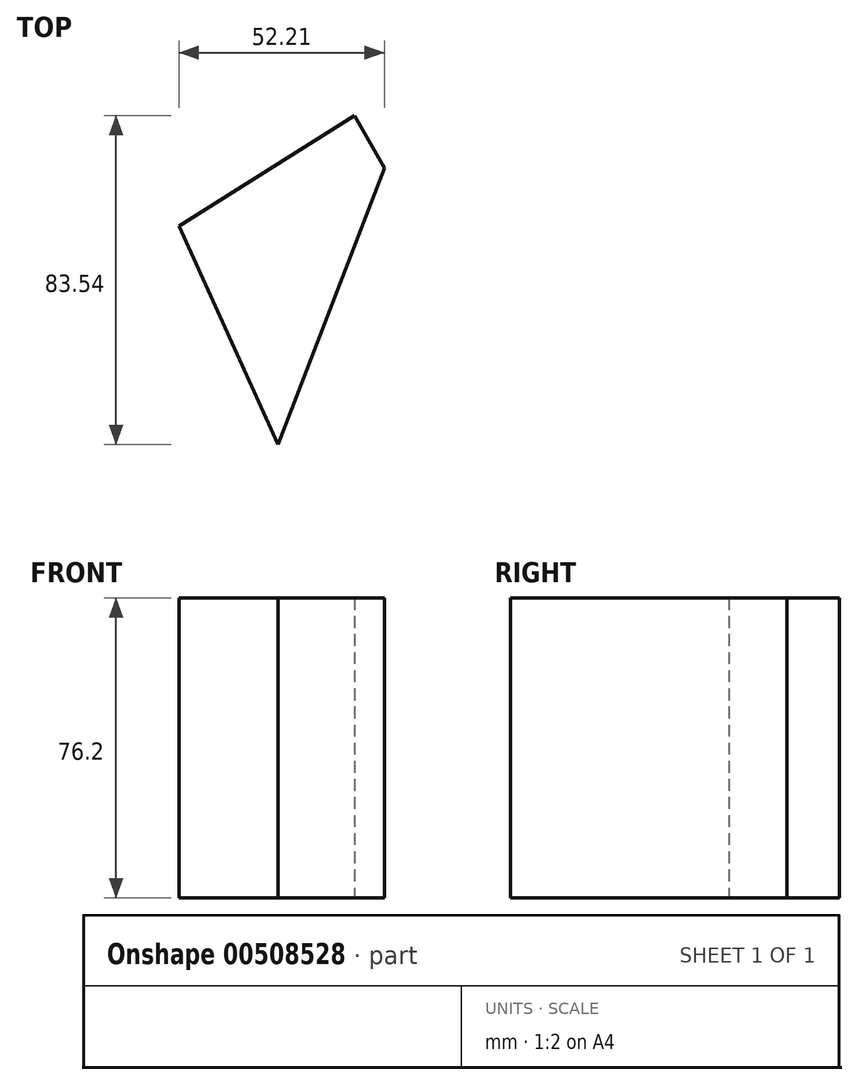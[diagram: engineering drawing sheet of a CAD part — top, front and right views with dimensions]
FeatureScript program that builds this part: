
annotation { "Feature Type Name" : "Feature", "Feature Type Description" : "" }
export const myFeature = defineFeature(function(context is Context, id is Id, definition is map)
    precondition{}
    {
        {
            var Q0;
            Q0=qCreatedBy(makeId("Top.planeOp"),FACE);
            var sketch = newSketch(context, id + "F0", { "sketchPlane" : qUnion([Q0])});
            skLineSegment(sketch, "E0", {"start": v(-44.6, 0) * mm, "end": v(0, 28.08) * mm});
            skLineSegment(sketch, "E1", {"start": v(-19.47, -55.46) * mm, "end": v(7.62, 14.82) * mm});
            skLineSegment(sketch, "E2", {"start": v(7.62, 14.82) * mm, "end": v(0, 28.08) * mm});
            skLineSegment(sketch, "E3", {"start": v(-44.6, 0) * mm, "end": v(-19.47, -55.46) * mm});
            skSolve(sketch);
        }
        {
            var Q0;
            Q0=makeQuery(id+"F0.imprint","IMPRINT",FACE,{"disambiguationData":[TD([[makeQuery(id+"F0.imprint","IMPRINT",EDGE,{"derivedFrom":sQuery(id+"F0.wireOp",EDGE,"E0")}),-1.0]])]});
            extrude(context, id + "F1", {"entities" : qUnion([Q0]), "depth" : 76.2 * mm});
        }
    });
